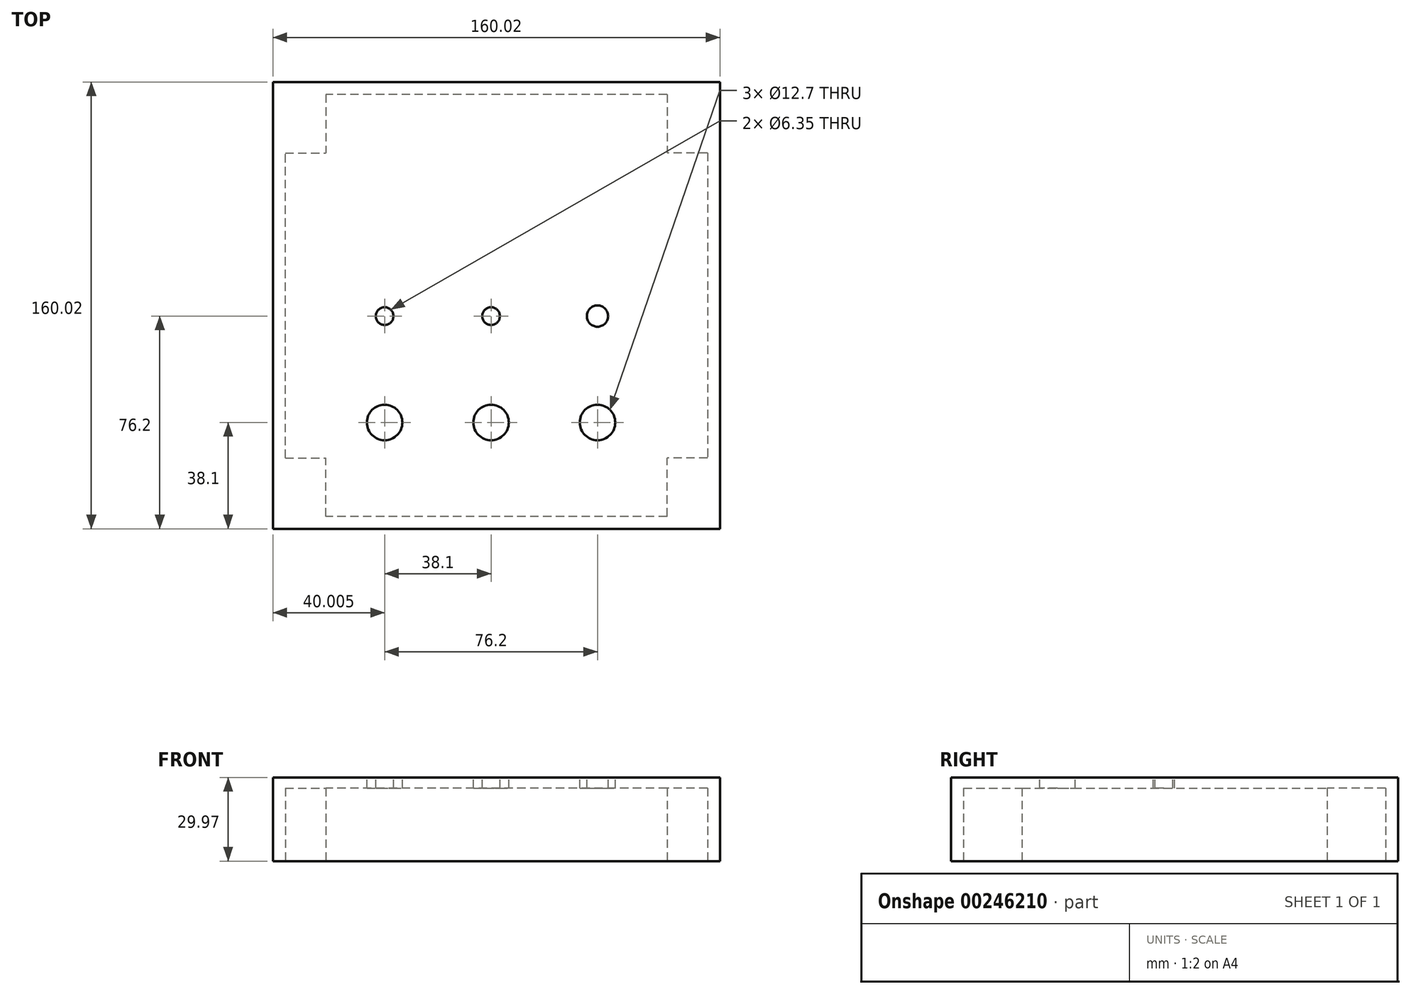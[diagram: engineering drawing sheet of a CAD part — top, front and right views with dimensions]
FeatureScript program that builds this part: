
annotation { "Feature Type Name" : "Feature", "Feature Type Description" : "" }
export const myFeature = defineFeature(function(context is Context, id is Id, definition is map)
    precondition{}
    {
        {
            var Q0;
            Q0=qCreatedBy(makeId("Top.planeOp"),FACE);
            var sketch = newSketch(context, id + "F0", { "sketchPlane" : qUnion([Q0])});
            skLineSegment(sketch, "E0.bottom", {"start": v(0, 0) * mm, "end": v(160.02, 0) * mm});
            skLineSegment(sketch, "E0.top", {"start": v(0, 160.02) * mm, "end": v(160.02, 160.02) * mm});
            skLineSegment(sketch, "E0.left", {"start": v(0, 0) * mm, "end": v(0, 160.02) * mm});
            skLineSegment(sketch, "E0.right", {"start": v(160.02, 0) * mm, "end": v(160.02, 160.02) * mm});
            skSolve(sketch);
        }
        {
            var Q0;
            Q0=qSketchRegion(id+"F0",true);
            extrude(context, id + "F1", {"entities" : qUnion([Q0]), "oppositeDirection" : true, "depth" : 29.97 * mm});
        }
        {
            var Q0;
            Q0=makeQuery(id+"F1.opExtrude","CAP_FACE",FACE,{"disambiguationData":[OSD([sQuery(id+"F0.wireOp",EDGE,"E0.bottom"),sQuery(id+"F0.wireOp",EDGE,"E0.top"),sQuery(id+"F0.wireOp",EDGE,"E0.left"),sQuery(id+"F0.wireOp",EDGE,"E0.right")])],"isStart":false});
            var sketch = newSketch(context, id + "F2", { "sketchPlane" : qUnion([Q0])});
            skLineSegment(sketch, "E1.bottom", {"start": v(0, 0) * mm, "end": v(18.92, 0) * mm});
            skLineSegment(sketch, "E1.top", {"start": v(4.45, -25.4) * mm, "end": v(18.92, -25.4) * mm});
            skLineSegment(sketch, "E1.left", {"start": v(0, 0) * mm, "end": v(0, -25.4) * mm});
            skLineSegment(sketch, "E1.right", {"start": v(18.92, -4.45) * mm, "end": v(18.92, -25.4) * mm});
            skLineSegment(sketch, "E2.bottom", {"start": v(0, -160.02) * mm, "end": v(18.92, -160.02) * mm});
            skLineSegment(sketch, "E2.top", {"start": v(4.45, -134.62) * mm, "end": v(18.92, -134.62) * mm});
            skLineSegment(sketch, "E2.left", {"start": v(0, -160.02) * mm, "end": v(0, -134.62) * mm});
            skLineSegment(sketch, "E2.right", {"start": v(18.92, -155.58) * mm, "end": v(18.92, -134.62) * mm});
            skLineSegment(sketch, "E3.bottom", {"start": v(160.02, 0) * mm, "end": v(141.1, 0) * mm});
            skLineSegment(sketch, "E3.top", {"start": v(155.58, -25.4) * mm, "end": v(141.1, -25.4) * mm});
            skLineSegment(sketch, "E3.left", {"start": v(160.02, 0) * mm, "end": v(160.02, -25.4) * mm});
            skLineSegment(sketch, "E3.right", {"start": v(141.1, -4.45) * mm, "end": v(141.1, -25.4) * mm});
            skLineSegment(sketch, "E4.bottom", {"start": v(160.02, -160.02) * mm, "end": v(141.1, -160.02) * mm});
            skLineSegment(sketch, "E4.top", {"start": v(155.58, -134.62) * mm, "end": v(141.1, -134.62) * mm});
            skLineSegment(sketch, "E4.left", {"start": v(160.02, -160.02) * mm, "end": v(160.02, -134.62) * mm});
            skLineSegment(sketch, "E4.right", {"start": v(141.1, -155.58) * mm, "end": v(141.1, -134.62) * mm});
            skLineSegment(sketch, "E5.left", {"start": v(160.02, -134.62) * mm, "end": v(160.02, -25.4) * mm});
            skLineSegment(sketch, "E5.right", {"start": v(155.58, -134.62) * mm, "end": v(155.58, -25.4) * mm});
            skLineSegment(sketch, "E6.bottom", {"start": v(141.1, 0) * mm, "end": v(18.92, 0) * mm});
            skLineSegment(sketch, "E6.top", {"start": v(141.1, -4.45) * mm, "end": v(18.92, -4.45) * mm});
            skLineSegment(sketch, "E7.left", {"start": v(0, -25.4) * mm, "end": v(0, -134.62) * mm});
            skLineSegment(sketch, "E7.right", {"start": v(4.45, -25.4) * mm, "end": v(4.45, -134.62) * mm});
            skLineSegment(sketch, "E8.bottom", {"start": v(141.1, -160.02) * mm, "end": v(18.92, -160.02) * mm});
            skLineSegment(sketch, "E8.top", {"start": v(141.1, -155.58) * mm, "end": v(18.92, -155.58) * mm});
            skSolve(sketch);
        }
        {
            var Q0;
            Q0=makeQuery(id+"F2.imprint","IMPRINT",FACE,{"disambiguationData":[TD([[makeQuery(id+"F2.imprint","IMPRINT",EDGE,{"derivedFrom":sQuery(id+"F2.wireOp",EDGE,"E1.top")}),-1.0]])]});
            extrude(context, id + "F3", {"entities" : qUnion([Q0]), "operationType" : NewBodyOperationType.REMOVE, "oppositeDirection" : true, "depth" : 26.16 * mm});
        }
        {
            var Q0;
            Q0=makeQuery(id+"F1.opExtrude","CAP_FACE",FACE,{"disambiguationData":[OSD([sQuery(id+"F0.wireOp",EDGE,"E0.bottom"),sQuery(id+"F0.wireOp",EDGE,"E0.top"),sQuery(id+"F0.wireOp",EDGE,"E0.left"),sQuery(id+"F0.wireOp",EDGE,"E0.right")])],"isStart":true});
            var sketch = newSketch(context, id + "F4", { "sketchPlane" : qUnion([Q0])});
            skCircle(sketch, "E9", {"center": v(40, 38.1) * mm, "radius": 6.35 * mm});
            skCircle(sketch, "E10.1.0.0", {"center": v(78.1, 38.1) * mm, "radius": 6.35 * mm});
            skCircle(sketch, "E10.2.0.0", {"center": v(116.2, 38.1) * mm, "radius": 6.35 * mm});
            skLineSegment(sketch, "E10.direction1", {"start": v(40, 38.1) * mm, "end": v(78.1, 38.1) * mm, "construction": true});
            skCircle(sketch, "E11", {"center": v(40, 76.2) * mm, "radius": 3.18 * mm});
            skCircle(sketch, "E12.1.0.0", {"center": v(78.1, 76.2) * mm, "radius": 3.18 * mm});
            skLineSegment(sketch, "E12.direction1", {"start": v(40, 76.2) * mm, "end": v(78.1, 76.2) * mm, "construction": true});
            skCircle(sketch, "E13", {"center": v(116.2, 76.2) * mm, "radius": 3.81 * mm});
            skSolve(sketch);
        }
        {
            var Q0;
            Q0=makeQuery(id+"F4.imprint","IMPRINT",FACE,{"disambiguationData":[TD([[makeQuery(id+"F4.imprint","IMPRINT",EDGE,{"derivedFrom":sQuery(id+"F4.wireOp",EDGE,"E9")}),1.0]])]});
            var Q1;
            Q1=makeQuery(id+"F4.imprint","IMPRINT",FACE,{"disambiguationData":[TD([[makeQuery(id+"F4.imprint","IMPRINT",EDGE,{"derivedFrom":sQuery(id+"F4.wireOp",EDGE,"E10.1.0.0")}),1.0]])]});
            var Q2;
            Q2=makeQuery(id+"F4.imprint","IMPRINT",FACE,{"disambiguationData":[TD([[makeQuery(id+"F4.imprint","IMPRINT",EDGE,{"derivedFrom":sQuery(id+"F4.wireOp",EDGE,"E10.2.0.0")}),1.0]])]});
            var Q3;
            Q3=makeQuery(id+"F4.imprint","IMPRINT",FACE,{"disambiguationData":[TD([[makeQuery(id+"F4.imprint","IMPRINT",EDGE,{"derivedFrom":sQuery(id+"F4.wireOp",EDGE,"E13")}),1.0]])]});
            var Q4;
            Q4=makeQuery(id+"F4.imprint","IMPRINT",FACE,{"disambiguationData":[TD([[makeQuery(id+"F4.imprint","IMPRINT",EDGE,{"derivedFrom":sQuery(id+"F4.wireOp",EDGE,"E12.1.0.0")}),1.0]])]});
            var Q5;
            Q5=makeQuery(id+"F4.imprint","IMPRINT",FACE,{"disambiguationData":[TD([[makeQuery(id+"F4.imprint","IMPRINT",EDGE,{"derivedFrom":sQuery(id+"F4.wireOp",EDGE,"E11")}),1.0]])]});
            extrude(context, id + "F5", {"entities" : qUnion([Q0, Q1, Q2, Q3, Q4, Q5]), "operationType" : NewBodyOperationType.REMOVE, "oppositeDirection" : true, "depth" : 6.35 * mm});
        }
    });
